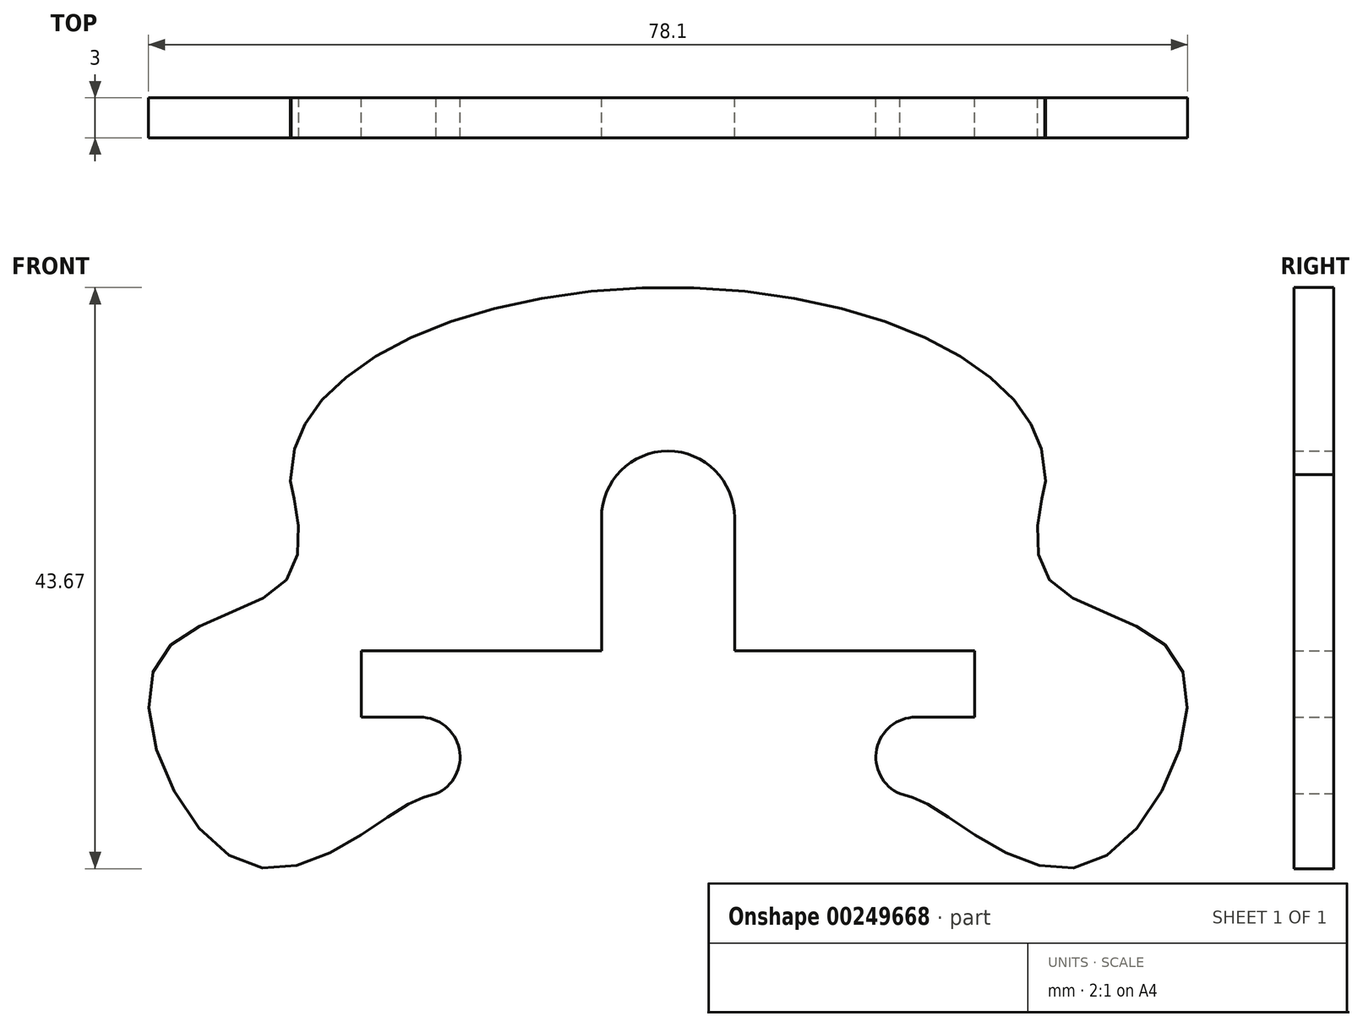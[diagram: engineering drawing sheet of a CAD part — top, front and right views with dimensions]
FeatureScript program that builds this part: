
annotation { "Feature Type Name" : "Feature", "Feature Type Description" : "" }
export const myFeature = defineFeature(function(context is Context, id is Id, definition is map)
    precondition{}
    {
        {
            var Q0;
            Q0=qCreatedBy(makeId("Front.planeOp"),FACE);
            var sketch = newSketch(context, id + "F0", { "sketchPlane" : qUnion([Q0])});
            skLineSegment(sketch, "E0", {"start": v(-23.06, -12.04) * mm, "end": v(-23.06, -7.04) * mm});
            skLineSegment(sketch, "E1", {"start": v(23.07, -12.04) * mm, "end": v(23.07, -7.04) * mm});
            skLineSegment(sketch, "E2", {"start": v(-23.06, -7.04) * mm, "end": v(-5, -7.04) * mm});
            skLineSegment(sketch, "E3", {"start": v(5, -7.04) * mm, "end": v(23.07, -7.04) * mm});
            skLineSegment(sketch, "E4", {"start": v(5, -7.04) * mm, "end": v(5, 2.96) * mm});
            skLineSegment(sketch, "E5", {"start": v(-5, -7.04) * mm, "end": v(-5, 2.96) * mm});
            skArc(sketch, "E6", {"start": v(5, 2.96) * mm, "mid": v(0, 7.96) * mm, "end": v(-5, 2.96) * mm});
            skLineSegment(sketch, "E7", {"start": v(-23.06, -12.04) * mm, "end": v(-18.63, -12.04) * mm});
            skFitSpline(sketch, "E8", {"points": [v(-28.33, 6.2) * mm, v(-28.38, 5.72) * mm, v(-28.4, -1.38) * mm, v(-38.48, -8.06) * mm, v(-31.58, -23.11) * mm, v(-20.2, -18.98) * mm, v(-17.44, -17.8) * mm]});
            skArc(sketch, "E9", {"start": v(-17.44, -17.8) * mm, "mid": v(-15.7, -14.43) * mm, "end": v(-18.63, -12.04) * mm});
            skLineSegment(sketch, "E10", {"start": v(23.07, -12.04) * mm, "end": v(18.63, -12.04) * mm});
            skFitSpline(sketch, "E11", {"points": [v(28.33, 6.2) * mm, v(28.38, 5.72) * mm, v(28.4, -1.38) * mm, v(38.48, -8.06) * mm, v(31.58, -23.11) * mm, v(20.2, -18.98) * mm, v(17.44, -17.8) * mm]});
            skArc(sketch, "E12", {"start": v(18.63, -12.04) * mm, "mid": v(15.7, -14.43) * mm, "end": v(17.44, -17.8) * mm});
            skEllipticalArc(sketch, "E13", {});
            const initialGuessF0  = {"E13": [0, 0.006202538000000004, 28.334969, 0, 0.028334969, 0.014048385, 0, 3.141593]};
            skSetInitialGuess(sketch, initialGuessF0);
            skSolve(sketch);
        }
        {
            var Q0;
            Q0=makeQuery(id+"F0.imprint","IMPRINT",FACE,{"disambiguationData":[TD([[makeQuery(id+"F0.imprint","IMPRINT",EDGE,{"derivedFrom":sQuery(id+"F0.wireOp",EDGE,"E0")}),1.0]])]});
            extrude(context, id + "F1", {"entities" : qUnion([Q0]), "depth" : 3 * mm});
        }
    });
